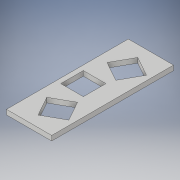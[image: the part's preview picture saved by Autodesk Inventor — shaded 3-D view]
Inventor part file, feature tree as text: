
AUTODESK INVENTOR PART (.ipt)
format: ipt  version: 2017 (Build 210142000, 142)  size: 123,392 bytes
history: native  units: in
note: dims shown in document units (in); Inventor stores cm internally (conversion verified against a paired STEP export)
features: sketch x2, extrude x2
ambient origin geometry x8: Origin, YZ Plane, XZ Plane, XY Plane, X Axis, Y Axis, Z Axis, Center Point
bodies: Body1 (feature_tree)
feature tree (4):
  sketch  "Sketch2"  dims[d11=2.9724in d28=0.1181in d29=0.0in]
  extrude  "Extrusion3"  Depth=0.1181in TaperAngle=0.0deg
  extrude  "Extrusion4"  Depth=0.5512in
  sketch  "Sketch6"  dims[d30=2.9528in d31=0.5512in d32=0.5512in d33=0.5512in d34=0.5512in d35=0.5512in d36=0.5512in d37=0.1969in d38=0.1969in d39=0.1181in d40=0.2756in d41=1.1024in d42=0.1181in d43=0.0in]
